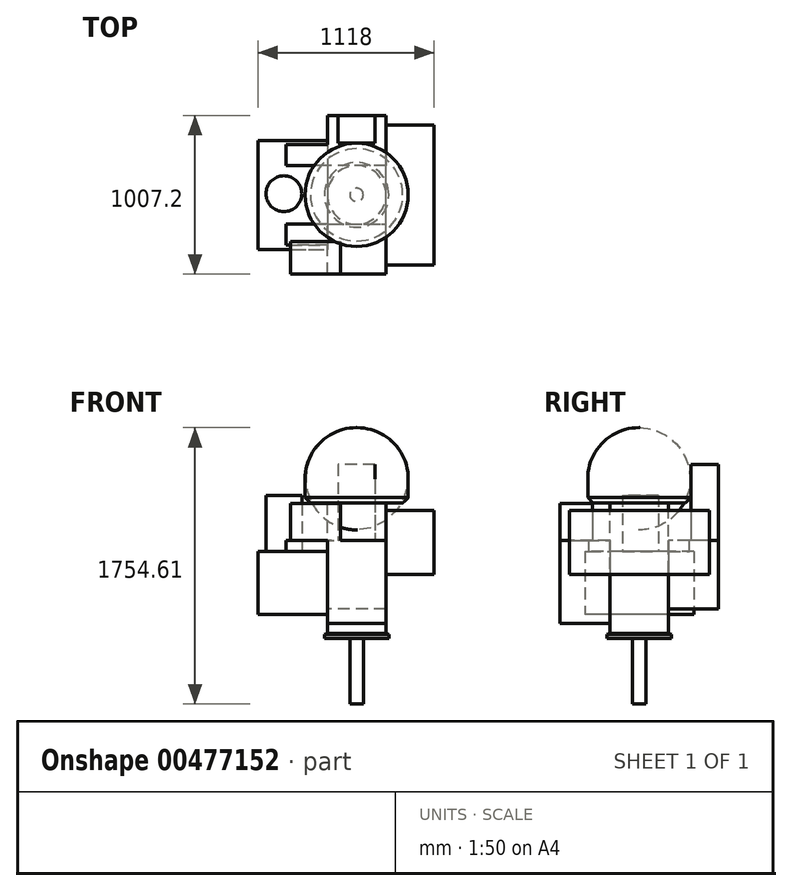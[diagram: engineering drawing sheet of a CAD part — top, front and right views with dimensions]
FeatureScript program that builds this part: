
annotation { "Feature Type Name" : "Feature", "Feature Type Description" : "" }
export const myFeature = defineFeature(function(context is Context, id is Id, definition is map)
    precondition{}
    {
        {
            var Q0;
            Q0=qCreatedBy(makeId("Front.planeOp"),FACE);
            var sketch = newSketch(context, id + "F0", { "sketchPlane" : qUnion([Q0])});
            skLineSegment(sketch, "E0", {"start": v(0, 0) * mm, "end": v(0, 25.3) * mm});
            skLineSegment(sketch, "E1", {"start": v(0, 25.3) * mm, "end": v(-18.9, 29.6) * mm});
            skLineSegment(sketch, "E2", {"start": v(-18.9, 29.6) * mm, "end": v(-18.9, 858.7) * mm});
            skLineSegment(sketch, "E3", {"start": v(-18.9, 858.7) * mm, "end": v(122.8, 858.7) * mm});
            skLineSegment(sketch, "E4", {"start": v(122.8, 858.7) * mm, "end": v(122.8, 1013) * mm});
            skLineSegment(sketch, "E5", {"start": v(-205, 1405.57) * mm, "end": v(-205, 307.85) * mm, "construction": true});
            skLineSegment(sketch, "E6", {"start": v(0, 0) * mm, "end": v(-205, 0) * mm});
            skPoint(sketch, "E7", {"position": v(-205, 1338) * mm});
            skArc(sketch, "E8", {"start": v(122.8, 1013) * mm, "mid": v(26.62, 1243.8) * mm, "end": v(-205, 1338) * mm});
            skLineSegment(sketch, "E9", {"start": v(-205, 1338) * mm, "end": v(-205, 0) * mm});
            skSolve(sketch);
        }
        {
            var Q0;
            Q0=makeQuery(id+"F0.imprint","IMPRINT",FACE,{"disambiguationData":[TD([[makeQuery(id+"F0.imprint","IMPRINT",EDGE,{"derivedFrom":sQuery(id+"F0.wireOp",EDGE,"E0")}),1.0]])]});
            var Q1;
            Q1=sQuery(id+"F0.wireOp",EDGE,"E5");
            revolve(context, id + "F1", {"entities" : qUnion([Q0]), "axis" : qUnion([Q1]), "revolveType" : RevolveType.FULL});
        }
        {
            var Q0;
            Q0=makeQuery(id+"F1.opRevolve","SWEPT_EDGE",EDGE,{"disambiguationData":[OSD([sQuery(id+"F0.wireOp",EDGE,"E3"),sQuery(id+"F0.wireOp",EDGE,"E4")])]});
            chamfer(context, id + "F2", {"entities" : qUnion([Q0]), "width" : 35 * mm, "tangentPropagation" : true});
        }
        {
            var Q0;
            Q0=makeQuery(id+"F1.opRevolve","SWEPT_EDGE",EDGE,{"disambiguationData":[OSD([sQuery(id+"F0.wireOp",EDGE,"E2"),sQuery(id+"F0.wireOp",EDGE,"E3")])]});
            fillet(context, id + "F3", {"entities" : qUnion([Q0]), "radius" : 8 * mm, "tangentPropagation" : true, "allowEdgeOverflow" : false});
        }
        {
            var Q0;
            Q0=makeQuery(id+"F1.opRevolve","SWEPT_FACE",FACE,{"disambiguationData":[OSD([sQuery(id+"F0.wireOp",EDGE,"E6")])]});
            var sketch = newSketch(context, id + "F4", { "sketchPlane" : qUnion([Q0])});
            skCircle(sketch, "E10", {"center": v(-205, 0) * mm, "radius": 42.3 * mm});
            skSolve(sketch);
        }
        {
            var Q0;
            Q0=makeQuery(id+"F4.imprint","IMPRINT",FACE,{"disambiguationData":[TD([[makeQuery(id+"F4.imprint","IMPRINT",EDGE,{"derivedFrom":sQuery(id+"F4.wireOp",EDGE,"E10")}),1.0]])]});
            extrude(context, id + "F5", {"entities" : qUnion([Q0]), "operationType" : NewBodyOperationType.ADD, "depth" : 416.6 * mm});
        }
        {
            var Q0;
            Q0=qCreatedBy(makeId("Right.planeOp"),FACE);
            cPlane(context, id + "F6", {"entities" : qUnion([Q0]), "cplaneType" : CPlaneType.OFFSET, "offset" : 18.9 * mm, "oppositeDirection" : true, "width" : 150 * mm, "height" : 150 * mm});
        }
        {
            var Q0;
            Q0=qCreatedBy(id+"F6.planeOp",FACE);
            var sketch = newSketch(context, id + "F7", { "sketchPlane" : qUnion([Q0])});
            skLineSegment(sketch, "E11.bottom", {"start": v(-445, 811.6) * mm, "end": v(445, 811.6) * mm});
            skLineSegment(sketch, "E11.top", {"start": v(-445, 405.8) * mm, "end": v(445, 405.8) * mm});
            skLineSegment(sketch, "E11.left", {"start": v(-445, 811.6) * mm, "end": v(-445, 405.8) * mm});
            skLineSegment(sketch, "E11.right", {"start": v(445, 811.6) * mm, "end": v(445, 405.8) * mm});
            skSolve(sketch);
        }
        {
            var Q0;
            Q0 = qSketchRegion(id + "F7", true);
            extrude(context, id + "F8", {"entities" : qUnion([Q0]), "operationType" : NewBodyOperationType.ADD, "depth" : 305.8 * mm});
        }
        {
            var Q0;
            Q0=qCreatedBy(id+"F6.planeOp",FACE);
            cPlane(context, id + "F9", {"entities" : qUnion([Q0]), "cplaneType" : CPlaneType.OFFSET, "offset" : 372.2 * mm, "oppositeDirection" : true, "width" : 150 * mm, "height" : 150 * mm});
        }
        {
            var Q0;
            Q0=qCreatedBy(id+"F9.planeOp",FACE);
            var sketch = newSketch(context, id + "F10", { "sketchPlane" : qUnion([Q0])});
            skLineSegment(sketch, "E12.bottom", {"start": v(346, 552.3) * mm, "end": v(-346, 552.3) * mm});
            skLineSegment(sketch, "E12.top", {"start": v(346, 150.6) * mm, "end": v(-346, 150.6) * mm});
            skLineSegment(sketch, "E12.left", {"start": v(346, 552.3) * mm, "end": v(346, 150.6) * mm});
            skLineSegment(sketch, "E12.right", {"start": v(-346, 552.3) * mm, "end": v(-346, 150.6) * mm});
            skSolve(sketch);
        }
        {
            var Q0;
            Q0 = qSketchRegion(id + "F10", true);
            extrude(context, id + "F11", {"entities" : qUnion([Q0]), "operationType" : NewBodyOperationType.ADD, "oppositeDirection" : true, "depth" : 440 * mm});
        }
        {
            var Q0;
            Q0=makeQuery(id+"F11.opExtrude","SWEPT_FACE",FACE,{"disambiguationData":[OSD([sQuery(id+"F10.wireOp",EDGE,"E12.bottom")])]});
            var sketch = newSketch(context, id + "F12", { "sketchPlane" : qUnion([Q0])});
            skCircle(sketch, "E13", {"center": v(-667.1, 7.5) * mm, "radius": 114 * mm});
            skSolve(sketch);
        }
        {
            var Q0;
            Q0 = qSketchRegion(id + "F12", true);
            extrude(context, id + "F13", {"entities" : qUnion([Q0]), "operationType" : NewBodyOperationType.ADD, "depth" : 356.5 * mm});
        }
        {
            var Q0;
            Q0=qCreatedBy(makeId("Front.planeOp"),FACE);
            cPlane(context, id + "F14", {"entities" : qUnion([Q0]), "cplaneType" : CPlaneType.OFFSET, "offset" : 186.1 * mm, "width" : 150 * mm, "height" : 150 * mm});
        }
        {
            var Q0;
            Q0=qCreatedBy(id+"F14.planeOp",FACE);
            var sketch = newSketch(context, id + "F15", { "sketchPlane" : qUnion([Q0])});
            skLineSegment(sketch, "E14.bottom", {"start": v(-391.1, 622.7) * mm, "end": v(-18.9, 622.7) * mm});
            skLineSegment(sketch, "E14.top", {"start": v(-391.1, 94.5) * mm, "end": v(-18.9, 94.5) * mm});
            skLineSegment(sketch, "E14.left", {"start": v(-391.1, 622.7) * mm, "end": v(-391.1, 94.5) * mm});
            skLineSegment(sketch, "E14.right", {"start": v(-18.9, 622.7) * mm, "end": v(-18.9, 94.5) * mm});
            skSolve(sketch);
        }
        {
            var Q0;
            Q0 = qSketchRegion(id + "F15", true);
            extrude(context, id + "F16", {"entities" : qUnion([Q0]), "depth" : 317.5 * mm});
        }
        {
            var Q0;
            Q0=qCreatedBy(makeId("Front.planeOp"),FACE);
            cPlane(context, id + "F17", {"entities" : qUnion([Q0]), "cplaneType" : CPlaneType.OFFSET, "offset" : 186.1 * mm, "oppositeDirection" : true, "width" : 150 * mm, "height" : 150 * mm});
        }
        {
            var Q0;
            Q0=qCreatedBy(id+"F17.planeOp",FACE);
            var sketch = newSketch(context, id + "F18", { "sketchPlane" : qUnion([Q0])});
            skLineSegment(sketch, "E15.bottom", {"start": v(-18.9, 621) * mm, "end": v(-391.1, 621) * mm});
            skLineSegment(sketch, "E15.top", {"start": v(-18.9, 186.6) * mm, "end": v(-391.1, 186.6) * mm});
            skLineSegment(sketch, "E15.left", {"start": v(-18.9, 621) * mm, "end": v(-18.9, 186.6) * mm});
            skLineSegment(sketch, "E15.right", {"start": v(-391.1, 621) * mm, "end": v(-391.1, 186.6) * mm});
            skSolve(sketch);
        }
        {
            var Q0;
            Q0 = qSketchRegion(id + "F18", true);
            extrude(context, id + "F19", {"entities" : qUnion([Q0]), "oppositeDirection" : true, "depth" : 317.5 * mm});
        }
        {
            var Q0;
            Q0=makeQuery(id+"F19.opExtrude","SWEPT_FACE",FACE,{"disambiguationData":[OSD([sQuery(id+"F18.wireOp",EDGE,"E15.bottom")])]});
            var sketch = newSketch(context, id + "F20", { "sketchPlane" : qUnion([Q0])});
            skLineSegment(sketch, "E16.bottom", {"start": v(-322, 503.6) * mm, "end": v(-88, 503.6) * mm});
            skLineSegment(sketch, "E16.top", {"start": v(-322, 327.8) * mm, "end": v(-88, 327.8) * mm});
            skLineSegment(sketch, "E16.left", {"start": v(-322, 503.6) * mm, "end": v(-322, 327.8) * mm});
            skLineSegment(sketch, "E16.right", {"start": v(-88, 503.6) * mm, "end": v(-88, 327.8) * mm});
            skSolve(sketch);
        }
        {
            var Q0;
            Q0 = qSketchRegion(id + "F20", true);
            extrude(context, id + "F21", {"entities" : qUnion([Q0]), "depth" : 484.6 * mm});
        }
        {
            var Q0;
            Q0=makeQuery(id+"F16.opExtrude","SWEPT_FACE",FACE,{"disambiguationData":[OSD([sQuery(id+"F15.wireOp",EDGE,"E14.bottom")])]});
            var sketch = newSketch(context, id + "F22", { "sketchPlane" : qUnion([Q0])});
            skLineSegment(sketch, "E17.bottom", {"start": v(-626, -297.6) * mm, "end": v(-308.5, -297.6) * mm});
            skLineSegment(sketch, "E17.top", {"start": v(-626, -503.6) * mm, "end": v(-308.5, -503.6) * mm});
            skLineSegment(sketch, "E17.left", {"start": v(-626, -297.6) * mm, "end": v(-626, -503.6) * mm});
            skLineSegment(sketch, "E17.right", {"start": v(-308.5, -297.6) * mm, "end": v(-308.5, -503.6) * mm});
            skSolve(sketch);
        }
        {
            var Q0;
            Q0 = qSketchRegion(id + "F22", true);
            extrude(context, id + "F23", {"entities" : qUnion([Q0]), "depth" : 234 * mm});
        }
        {
            var Q0;
            Q0=makeQuery(id+"F19.opExtrude","SWEPT_FACE",FACE,{"disambiguationData":[OSD([sQuery(id+"F18.wireOp",EDGE,"E15.bottom")])]});
            var sketch = newSketch(context, id + "F24", { "sketchPlane" : qUnion([Q0])});
            skLineSegment(sketch, "E18.bottom", {"start": v(-652.9, 318.2) * mm, "end": v(-391.1, 318.2) * mm});
            skLineSegment(sketch, "E18.top", {"start": v(-652.9, 186.1) * mm, "end": v(-391.1, 186.1) * mm});
            skLineSegment(sketch, "E18.left", {"start": v(-652.9, 318.2) * mm, "end": v(-652.9, 186.1) * mm});
            skLineSegment(sketch, "E18.right", {"start": v(-391.1, 318.2) * mm, "end": v(-391.1, 186.1) * mm});
            skSolve(sketch);
        }
        {
            var Q0;
            Q0 = qSketchRegion(id + "F24", true);
            extrude(context, id + "F25", {"entities" : qUnion([Q0]), "operationType" : NewBodyOperationType.ADD, "endBound" : BoundingType.UP_TO_NEXT, "oppositeDirection" : true, "depth" : 25 * mm});
        }
        {
            var Q0;
            Q0=makeQuery(id+"F16.opExtrude","SWEPT_FACE",FACE,{"disambiguationData":[OSD([sQuery(id+"F15.wireOp",EDGE,"E14.bottom")])]});
            var sketch = newSketch(context, id + "F26", { "sketchPlane" : qUnion([Q0])});
            skLineSegment(sketch, "E19.bottom", {"start": v(-652.9, -186.1) * mm, "end": v(-391.1, -186.1) * mm});
            skLineSegment(sketch, "E19.top", {"start": v(-652.9, -318.2) * mm, "end": v(-391.1, -318.2) * mm});
            skLineSegment(sketch, "E19.left", {"start": v(-652.9, -186.1) * mm, "end": v(-652.9, -318.2) * mm});
            skLineSegment(sketch, "E19.right", {"start": v(-391.1, -186.1) * mm, "end": v(-391.1, -318.2) * mm});
            skSolve(sketch);
        }
        {
            var Q0;
            Q0 = qSketchRegion(id + "F26", true);
            extrude(context, id + "F27", {"entities" : qUnion([Q0]), "operationType" : NewBodyOperationType.ADD, "endBound" : BoundingType.UP_TO_NEXT, "oppositeDirection" : true, "depth" : 25 * mm});
        }
    });
